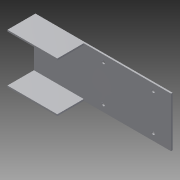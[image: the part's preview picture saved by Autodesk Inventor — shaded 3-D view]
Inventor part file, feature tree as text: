
AUTODESK INVENTOR PART (.ipt)
format: ipt  version: 2013 (Build 170138000, 138)  size: 103,936 bytes
history: native  units: in
note: dims shown in document units (in); Inventor stores cm internally (conversion verified against a paired STEP export)
features: other x4, reference x4, sketch x2, extrude x1, hole x1
ambient origin geometry x8: Origin, YZ Plane, XZ Plane, XY Plane, X Axis, Y Axis, Z Axis, Center Point
bodies: Solid1 (feature_tree)
feature tree (12):
  other  "Table"
  other  "channel2.25x4.ipt"
  extrude  "Extrusion1"  TaperAngle=0.0deg  [1 undecoded]
  hole  "Hole1"  [1 undecoded]
  other  "Solid1::channel2.25x4.ipt"
  other  "TaggingFeature1"
  sketch  "Sketch1"  dims[d0=4.0in d1=2.25in d2=0.125in d4=0.0in]
  sketch  "Sketch2"  dims[d5=1.0in d6=0.0in d7=4.0in d8=0.26in d9=0.75in d10=0.375in d11=0.25in d12=0.5635in d13=1.0in d14=0.8108in]
  reference  "Reference1"
  reference  "Reference2"
  reference  "Reference3"
  reference  "Reference4"
note: 2 required parameter values undecoded (feature->parameter linkage not recoverable at this tier; creation-order binding heuristic only, values carry confidence <= 0.55)
